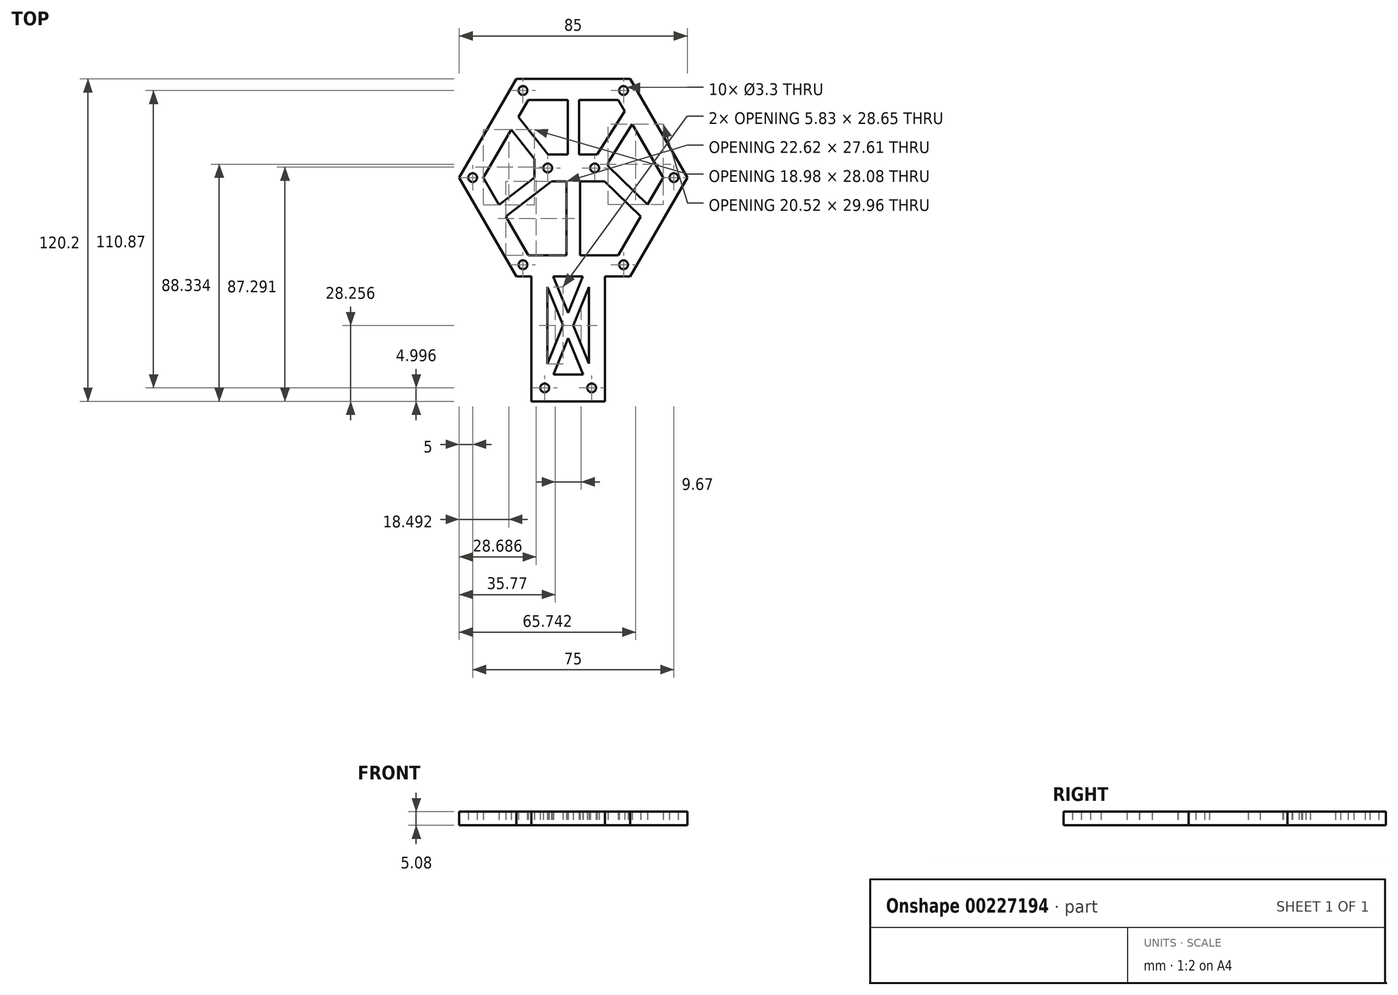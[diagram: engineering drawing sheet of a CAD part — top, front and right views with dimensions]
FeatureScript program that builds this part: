
annotation { "Feature Type Name" : "Feature", "Feature Type Description" : "" }
export const myFeature = defineFeature(function(context is Context, id is Id, definition is map)
    precondition{}
    {
        {
            var Q0;
            Q0=qCreatedBy(makeId("Top.planeOp"),FACE);
            var sketch = newSketch(context, id + "F0", { "sketchPlane" : qUnion([Q0])});
            skCircle(sketch, "E0.cCircle", {"center": v(0, 0) * mm, "radius": 32.48 * mm, "construction": true});
            skLineSegment(sketch, "E0.0", {"start": v(-18.75, 32.48) * mm, "end": v(18.75, 32.48) * mm, "construction": true});
            skLineSegment(sketch, "E0.1", {"start": v(18.75, 32.48) * mm, "end": v(37.5, 0) * mm, "construction": true});
            skLineSegment(sketch, "E0.2", {"start": v(37.5, 0) * mm, "end": v(18.75, -32.48) * mm, "construction": true});
            skLineSegment(sketch, "E0.3", {"start": v(18.75, -32.48) * mm, "end": v(-18.75, -32.48) * mm, "construction": true});
            skLineSegment(sketch, "E0.4", {"start": v(-18.75, -32.48) * mm, "end": v(-37.5, 0) * mm, "construction": true});
            skLineSegment(sketch, "E0.5", {"start": v(-37.5, 0) * mm, "end": v(-18.75, 32.48) * mm, "construction": true});
            skPoint(sketch, "E0.0.midPoint", {"position": v(0, 32.48) * mm});
            skCircle(sketch, "E1", {"center": v(-18.75, 32.48) * mm, "radius": 1.65 * mm});
            skCircle(sketch, "E2", {"center": v(18.75, 32.48) * mm, "radius": 1.65 * mm});
            skCircle(sketch, "E3", {"center": v(37.5, 0) * mm, "radius": 1.65 * mm});
            skCircle(sketch, "E4", {"center": v(18.75, -32.48) * mm, "radius": 1.65 * mm});
            skCircle(sketch, "E5", {"center": v(-18.75, -32.48) * mm, "radius": 1.65 * mm});
            skCircle(sketch, "E6", {"center": v(-37.5, 0) * mm, "radius": 1.65 * mm});
            skCircle(sketch, "E7.cCircle", {"center": v(0, 0) * mm, "radius": 36.8 * mm, "construction": true});
            skLineSegment(sketch, "E7.0", {"start": v(-21.25, 36.8) * mm, "end": v(21.25, 36.8) * mm});
            skLineSegment(sketch, "E7.1", {"start": v(21.25, 36.8) * mm, "end": v(42.5, 0) * mm});
            skLineSegment(sketch, "E7.2", {"start": v(42.5, 0) * mm, "end": v(21.25, -36.8) * mm});
            skLineSegment(sketch, "E7.3", {"start": v(21.25, -36.8) * mm, "end": v(-21.25, -36.8) * mm});
            skLineSegment(sketch, "E7.4", {"start": v(-21.25, -36.8) * mm, "end": v(-42.5, 0) * mm});
            skLineSegment(sketch, "E7.5", {"start": v(-42.5, 0) * mm, "end": v(-21.25, 36.8) * mm});
            skPoint(sketch, "E7.0.midPoint", {"position": v(0, 36.8) * mm});
            skCircle(sketch, "E8.cCircle", {"center": v(0, 0) * mm, "radius": 29.01 * mm, "construction": true});
            skLineSegment(sketch, "E8.0", {"start": v(-16.75, 29.01) * mm, "end": v(16.75, 29.01) * mm});
            skLineSegment(sketch, "E8.1", {"start": v(16.75, 29.01) * mm, "end": v(33.5, 0) * mm});
            skLineSegment(sketch, "E8.2", {"start": v(33.5, 0) * mm, "end": v(16.75, -29.01) * mm});
            skLineSegment(sketch, "E8.3", {"start": v(16.75, -29.01) * mm, "end": v(-16.75, -29.01) * mm});
            skLineSegment(sketch, "E8.4", {"start": v(-16.75, -29.01) * mm, "end": v(-33.5, 0) * mm});
            skLineSegment(sketch, "E8.5", {"start": v(-33.5, 0) * mm, "end": v(-16.75, 29.01) * mm});
            skPoint(sketch, "E8.0.midPoint", {"position": v(0, 29.01) * mm});
            skLineSegment(sketch, "E9", {"start": v(-9.52, 3.6) * mm, "end": v(7.98, 3.6) * mm, "construction": true});
            skLineSegment(sketch, "E10", {"start": v(-10.65, -78.4) * mm, "end": v(6.85, -78.4) * mm, "construction": true});
            skCircle(sketch, "E11", {"center": v(-9.52, 3.6) * mm, "radius": 1.65 * mm});
            skCircle(sketch, "E12", {"center": v(7.98, 3.6) * mm, "radius": 1.65 * mm});
            skCircle(sketch, "E13", {"center": v(-10.65, -78.4) * mm, "radius": 1.65 * mm});
            skCircle(sketch, "E14", {"center": v(6.85, -78.4) * mm, "radius": 1.65 * mm});
            skLineSegment(sketch, "E15.bottom", {"start": v(-14.52, 8.6) * mm, "end": v(12.98, 8.6) * mm});
            skLineSegment(sketch, "E15.top", {"start": v(-14.52, -1.4) * mm, "end": v(12.98, -1.4) * mm});
            skLineSegment(sketch, "E15.left", {"start": v(-14.52, 8.6) * mm, "end": v(-14.52, -1.4) * mm});
            skLineSegment(sketch, "E15.right", {"start": v(12.98, 8.6) * mm, "end": v(12.98, -1.4) * mm});
            skPoint(sketch, "E15.middle", {"position": v(-0.77, 3.6) * mm});
            skLineSegment(sketch, "E16.bottom", {"start": v(-15.65, -73.4) * mm, "end": v(11.85, -73.4) * mm});
            skLineSegment(sketch, "E16.top", {"start": v(-15.65, -83.4) * mm, "end": v(11.85, -83.4) * mm});
            skLineSegment(sketch, "E16.left", {"start": v(-15.65, -73.4) * mm, "end": v(-15.65, -83.4) * mm});
            skLineSegment(sketch, "E16.right", {"start": v(11.85, -73.4) * mm, "end": v(11.85, -83.4) * mm});
            skPoint(sketch, "E16.middle", {"position": v(-1.9, -78.4) * mm});
            skLineSegment(sketch, "E17", {"start": v(-15.65, -73.4) * mm, "end": v(-15.65, -36.8) * mm});
            skLineSegment(sketch, "E18", {"start": v(-9.65, -73.4) * mm, "end": v(-9.65, -36.8) * mm});
            skLineSegment(sketch, "E19", {"start": v(11.85, -73.4) * mm, "end": v(11.85, -36.8) * mm});
            skLineSegment(sketch, "E20", {"start": v(5.85, -73.4) * mm, "end": v(5.85, -36.8) * mm});
            skLineSegment(sketch, "E21", {"start": v(5.85, -55.1) * mm, "end": v(11.85, -55.1) * mm, "construction": true});
            skLineSegment(sketch, "E22", {"start": v(-15.65, -55.1) * mm, "end": v(-9.65, -55.1) * mm, "construction": true});
            skLineSegment(sketch, "E23", {"start": v(-7.5, -36.8) * mm, "end": v(5.85, -69.4) * mm});
            skLineSegment(sketch, "E24", {"start": v(5.85, -40.74) * mm, "end": v(-7.34, -73.4) * mm});
            skLineSegment(sketch, "E25", {"start": v(-9.65, -55.1) * mm, "end": v(5.85, -55.1) * mm, "construction": true});
            skLineSegment(sketch, "E26.1.0", {"start": v(3.71, -73.4) * mm, "end": v(-9.65, -40.8) * mm});
            skLineSegment(sketch, "E26.1.1", {"start": v(-9.65, -69.46) * mm, "end": v(3.55, -36.8) * mm});
            skPoint(sketch, "E26.center", {"position": v(-1.9, -55.1) * mm});
            skLineSegment(sketch, "E27", {"start": v(-9.44, 8.6) * mm, "end": v(-20.45, 22.6) * mm});
            skLineSegment(sketch, "E28", {"start": v(-14.52, 6.96) * mm, "end": v(-23.14, 17.94) * mm});
            skLineSegment(sketch, "E29", {"start": v(8.94, 8.6) * mm, "end": v(19.17, 24.82) * mm});
            skLineSegment(sketch, "E30", {"start": v(12.98, 5.63) * mm, "end": v(22, 19.92) * mm});
            skLineSegment(sketch, "E31", {"start": v(12.98, 4.38) * mm, "end": v(27.7, -10.04) * mm});
            skLineSegment(sketch, "E32", {"start": v(11.75, -1.4) * mm, "end": v(25.12, -14.5) * mm});
            skLineSegment(sketch, "E33", {"start": v(-8.15, -1.4) * mm, "end": v(-25.12, -14.5) * mm});
            skLineSegment(sketch, "E34", {"start": v(-14.52, 0) * mm, "end": v(-27.65, -10.14) * mm});
            skLineSegment(sketch, "E35", {"start": v(-20.16, -4.36) * mm, "end": v(-17.1, -8.32) * mm, "construction": true});
            skLineSegment(sketch, "E36", {"start": v(16.3, -5.86) * mm, "end": v(19.8, -2.29) * mm, "construction": true});
            skLineSegment(sketch, "E37", {"start": v(16.82, 11.7) * mm, "end": v(12.59, 14.38) * mm, "construction": true});
            skLineSegment(sketch, "E38", {"start": v(-18.24, 11.7) * mm, "end": v(-14.3, 14.79) * mm, "construction": true});
            skLineSegment(sketch, "E39", {"start": v(-2.5, -1.4) * mm, "end": v(-2.5, -29.01) * mm});
            skLineSegment(sketch, "E40", {"start": v(2.5, -1.4) * mm, "end": v(2.5, -29.01) * mm});
            skLineSegment(sketch, "E41", {"start": v(-2.5, -10.42) * mm, "end": v(2.5, -10.42) * mm, "construction": true});
            skLineSegment(sketch, "E42", {"start": v(-2.08, 8.6) * mm, "end": v(-2.08, 29.01) * mm});
            skLineSegment(sketch, "E43", {"start": v(2.2, 8.6) * mm, "end": v(2.2, 29.01) * mm});
            skLineSegment(sketch, "E44", {"start": v(-2.08, 18.8) * mm, "end": v(2.2, 18.8) * mm, "construction": true});
            skSolve(sketch);
        }
        {
            var Q0;
            Q0=makeQuery(id+"F0.imprint","IMPRINT",FACE,{"disambiguationData":[TD([[makeQuery(id+"F0.imprint","IMPRINT",EDGE,{"derivedFrom":sQuery(id+"F0.wireOp",EDGE,"E1")}),-1.0]])]});
            var Q1;
            {var subQ4=sQuery(id+"F0.wireOp",EDGE,"9ny764Z0-yEnc-nTom-sgEr-T5m8jRU7CaOd");Q1=makeQuery(id+"F0.imprint","IMPRINT",FACE,{"disambiguationData":[TD([[makeQuery(id+"F0.imprint","IMPRINT",EDGE,{"derivedFrom":subQ4}),1.0]])]});}
            var Q2;
            {var subQ0=sQuery(id+"F0.wireOp",EDGE,"mveJp2gq-viMz-v7hY-WbP1-sUx4nALb4Kya");Q2=makeQuery(id+"F0.imprint","IMPRINT",FACE,{"disambiguationData":[TD([[makeQuery(id+"F0.imprint","IMPRINT",EDGE,{"derivedFrom":subQ0}),-1.0]])]});}
            var Q3;
            {var subQ0=sQuery(id+"F0.wireOp",EDGE,"Fl41E3Zq-ps3j-7aEv-HD6p-v4TBVcw58FQC");Q3=makeQuery(id+"F0.imprint","IMPRINT",FACE,{"disambiguationData":[TD([[makeQuery(id+"F0.imprint","IMPRINT",EDGE,{"derivedFrom":subQ0}),1.0]])]});}
            var Q4;
            Q4=makeQuery(id+"F0.imprint","IMPRINT",FACE,{"disambiguationData":[TD([[makeQuery(id+"F0.imprint","IMPRINT",EDGE,{"derivedFrom":sQuery(id+"F0.wireOp",EDGE,"E11")}),-1.0]])]});
            var Q5;
            {var subQ0=sQuery(id+"F0.wireOp",EDGE,"ZUoPdMyJ-yNmC-lj2F-qgpw-CtUOoCRU5N7t");Q5=makeQuery(id+"F0.imprint","IMPRINT",FACE,{"disambiguationData":[TD([[makeQuery(id+"F0.imprint","IMPRINT",EDGE,{"derivedFrom":subQ0}),1.0]])]});}
            var Q6;
            {var subQ4=sQuery(id+"F0.wireOp",EDGE,"E17");Q6=makeQuery(id+"F0.imprint","IMPRINT",FACE,{"disambiguationData":[TD([[makeQuery(id+"F0.imprint","IMPRINT",EDGE,{"derivedFrom":subQ4}),-1.0]])]});}
            var Q7;
            {var subQ4=sQuery(id+"F0.wireOp",EDGE,"E19");Q7=makeQuery(id+"F0.imprint","IMPRINT",FACE,{"disambiguationData":[TD([[makeQuery(id+"F0.imprint","IMPRINT",EDGE,{"derivedFrom":subQ4}),1.0]])]});}
            var Q8;
            {var subQ1=sQuery(id+"F0.wireOp",EDGE,"E20");var subQ7=sQuery(id+"F0.wireOp",EDGE,"E7.3");var subQ8=makeQuery(id+"F0.imprint","INTERSECT",VERTEX,{"derivedFrom":[subQ7,subQ1]});Q8=makeQuery(id+"F0.imprint","IMPRINT",FACE,{"disambiguationData":[TD([[makeQuery(id+"F0.imprint","IMPRINT",EDGE,{"disambiguationData":[TD([[subQ8,-1.0]])],"derivedFrom":subQ7}),1.0]])]});}
            var Q9;
            {var subQ1=sQuery(id+"F0.wireOp",EDGE,"E18");var subQ6=sQuery(id+"F0.wireOp",EDGE,"E7.3");var subQ9=makeQuery(id+"F0.imprint","INTERSECT",VERTEX,{"derivedFrom":[subQ6,subQ1]});Q9=makeQuery(id+"F0.imprint","IMPRINT",FACE,{"disambiguationData":[TD([[makeQuery(id+"F0.imprint","IMPRINT",EDGE,{"disambiguationData":[TD([[subQ9,1.0]])],"derivedFrom":subQ6}),1.0]])]});}
            var Q10;
            {var subQ0=sQuery(id+"F0.wireOp",EDGE,"E26.1.1");var subQ1=sQuery(id+"F0.wireOp",EDGE,"E23");var subQ2=makeQuery(id+"F0.imprint","INTERSECT",VERTEX,{"derivedFrom":[subQ1,subQ0]});Q10=makeQuery(id+"F0.imprint","IMPRINT",FACE,{"disambiguationData":[TD([[makeQuery(id+"F0.imprint","IMPRINT",EDGE,{"disambiguationData":[TD([[subQ2,-1.0]])],"derivedFrom":subQ1}),-1.0]])]});}
            var Q11;
            {var subQ5=sQuery(id+"F0.wireOp",EDGE,"E18");var subQ6=sQuery(id+"F0.wireOp",EDGE,"E16.bottom");var subQ7=makeQuery(id+"F0.imprint","INTERSECT",VERTEX,{"derivedFrom":[subQ6,subQ5]});Q11=makeQuery(id+"F0.imprint","IMPRINT",FACE,{"disambiguationData":[TD([[makeQuery(id+"F0.imprint","IMPRINT",EDGE,{"disambiguationData":[TD([[subQ7,-1.0]])],"derivedFrom":subQ6}),1.0]])]});}
            var Q12;
            {var subQ5=sQuery(id+"F0.wireOp",EDGE,"E20");var subQ7=sQuery(id+"F0.wireOp",EDGE,"E16.bottom");var subQ8=makeQuery(id+"F0.imprint","INTERSECT",VERTEX,{"derivedFrom":[subQ7,subQ5]});Q12=makeQuery(id+"F0.imprint","IMPRINT",FACE,{"disambiguationData":[TD([[makeQuery(id+"F0.imprint","IMPRINT",EDGE,{"disambiguationData":[TD([[subQ8,1.0]])],"derivedFrom":subQ7}),1.0]])]});}
            var Q13;
            Q13=makeQuery(id+"F0.imprint","IMPRINT",FACE,{"disambiguationData":[TD([[makeQuery(id+"F0.imprint","IMPRINT",EDGE,{"derivedFrom":sQuery(id+"F0.wireOp",EDGE,"E13")}),-1.0]])]});
            var Q14;
            {var subQ4=sQuery(id+"F0.wireOp",EDGE,"E27");Q14=makeQuery(id+"F0.imprint","IMPRINT",FACE,{"disambiguationData":[TD([[makeQuery(id+"F0.imprint","IMPRINT",EDGE,{"derivedFrom":subQ4}),1.0]])]});}
            var Q15;
            {var subQ0=sQuery(id+"F0.wireOp",EDGE,"E42");Q15=makeQuery(id+"F0.imprint","IMPRINT",FACE,{"disambiguationData":[TD([[makeQuery(id+"F0.imprint","IMPRINT",EDGE,{"derivedFrom":subQ0}),-1.0]])]});}
            var Q16;
            {var subQ0=sQuery(id+"F0.wireOp",EDGE,"E29");Q16=makeQuery(id+"F0.imprint","IMPRINT",FACE,{"disambiguationData":[TD([[makeQuery(id+"F0.imprint","IMPRINT",EDGE,{"derivedFrom":subQ0}),-1.0]])]});}
            var Q17;
            {var subQ0=sQuery(id+"F0.wireOp",EDGE,"E31");Q17=makeQuery(id+"F0.imprint","IMPRINT",FACE,{"disambiguationData":[TD([[makeQuery(id+"F0.imprint","IMPRINT",EDGE,{"derivedFrom":subQ0}),-1.0]])]});}
            var Q18;
            {var subQ4=sQuery(id+"F0.wireOp",EDGE,"E33");Q18=makeQuery(id+"F0.imprint","IMPRINT",FACE,{"disambiguationData":[TD([[makeQuery(id+"F0.imprint","IMPRINT",EDGE,{"derivedFrom":subQ4}),-1.0]])]});}
            var Q19;
            {var subQ0=sQuery(id+"F0.wireOp",EDGE,"E39");Q19=makeQuery(id+"F0.imprint","IMPRINT",FACE,{"disambiguationData":[TD([[makeQuery(id+"F0.imprint","IMPRINT",EDGE,{"derivedFrom":subQ0}),1.0]])]});}
            extrude(context, id + "F1", {"entities" : qUnion([Q0, Q1, Q2, Q3, Q4, Q5, Q6, Q7, Q8, Q9, Q10, Q11, Q12, Q13, Q14, Q15, Q16, Q17, Q18, Q19]), "depth" : 5.08 * mm});
        }
    });
